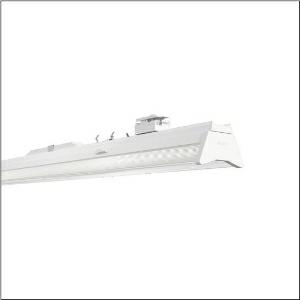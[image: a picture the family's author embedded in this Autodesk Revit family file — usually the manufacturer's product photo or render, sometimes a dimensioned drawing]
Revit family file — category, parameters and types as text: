
# Revit family: licross_r__21_performance_mo_52td16dn46xg_ca4f
name_source: partatom
category: Lighting Fixtures
units: mm (PartAtom-declared; Revit-internal decimal feet)

## family parameters
Cut with Voids When Loaded = No
Host = Face
Light Source = No
Part Type = Normal
Room Calculation Point = No
Round Connector Dimension = Use Diameter
Shared = No

## types (1)
- --- (1 x LED, 6000 lm, 32.7 W, 4000K)
    Apparent Load = 33 VA
    CIE Flux Codes = 66 88 96 79 100
    Color Rendering = 80
    Color Temperature = 4000K
    Default Elevation = 1800 mm
    Description = Licross® 21 Performance MO, luminaire insert, of sheet steel, galvanised, coil coated, white, length: 1.500mm, width: 120mm, height: 123mm, LED rated luminous flux: 6.000lm, light colour: 840, control gear: DALI 2, with plug, 5-pole, with phase selection, mains connection: 220..240V, AC, 50/60Hz, rated input power: 33W, internal wiring halogen-free, primary light control with lens, of plastic, primary optical cover: cover, of PMMA, light emission: direct/indirect distribution, primary light characteristic: symmetric, protection rating (complete): IP54, insulation class (complete): insulation class I (protective earthing), certification: CE, ENEC, VDE, UKCA, protection symbol: D if used in an environment with non-conductive dust loads with corresponding accessories, impact resistance: IK06, permissible ambient temperature for indoor applications: -25..+45°C, corresponds to IFS (International Featured Standards) requirements for safety and quality in the food industry, reducing of maximum allowable ambient temperature of 5°C with ceiling mounting, LABS conformity tested according to VDMA 24364:2018-05, packaging unit: 1 piece
    Height = 114 mm
    Lamp = 1 x LED
    Lamp Light Flux = 6000 lm
    Lamp Power = 32.7 W
    Lamp count = 1
    Length = 1500 mm
    Luminous efficacy = 183 lm/W
    Manufacturer = Siteco
    ModVariant = No
    Model = 52TD16DN46XG
    Mounting Place = Ceiling
    Mounting Type = Pendant
    Number of Poles = 1
    OnlyDefault = Yes
    Power Factor = 1
    Product Name = Licross® 21 Performance MO
    Product group = luminaire insert | ceiling pendant
    ProductGroupID = 902
    Protection Class = Protection class I
    Protection Degree = IP 54
    RLX_Detail_Level = 1
    RLX_Emergency_Light_Flux = 0 lm
    RLX_Emergency_Type = 0
    RLX_Emergency_Type_DB = No
    RlxData = <blob elided: 33669 chars, md5=c1afdf13>
    Socket = socket
    Standby Power = 0 W
    System Light Flux = 6000 lm
    System Power = 33 W
    Type Comments = factory setting: luminous flux: 100 % | dim-lin: 254 | 222 mA
    Type Image = l_1256138.jpg
    URL = http://relux.com
    VarID = @adj_150709
    Voltage = 0 V
    Weight = 0.00 kg
    Width = 120 mm

## geometry (parser evidence)
native form markers: Blend x4, Sweep x11
no freeform markers — native parametric forms only
